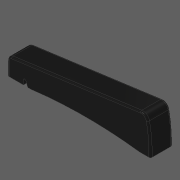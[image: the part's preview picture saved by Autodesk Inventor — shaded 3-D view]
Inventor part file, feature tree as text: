
AUTODESK INVENTOR PART (.ipt)
format: ipt  version: 2020 (Build 240168000, 168)  size: 275,456 bytes
history: native  units: in
note: dims shown in document units (in); Inventor stores cm internally (conversion verified against a paired STEP export)
features: other x3, extrude x3, fillet x2
ambient origin geometry x8: Origin, YZ Plane, XZ Plane, XY Plane, X Axis, Y Axis, Z Axis, Center Point
bodies: Solid1 (feature_tree)
feature tree (8):
  other  "Slot Start Plane"
  other  "Key Profile"
  extrude  "Key"  Depth=0.0787in
  extrude  "Protrusion Cutout"  TaperAngle=0.0deg  [1 undecoded]
  fillet  "Front Fillet"  [1 undecoded]
  extrude  "Slot"  Depth=0.1181in
  fillet  "Edge Softening"  Radius=0.1374in
  other  "Slot Sketch"
note: 2 required parameter values undecoded (feature->parameter linkage not recoverable at this tier; creation-order binding heuristic only, values carry confidence <= 0.55)
